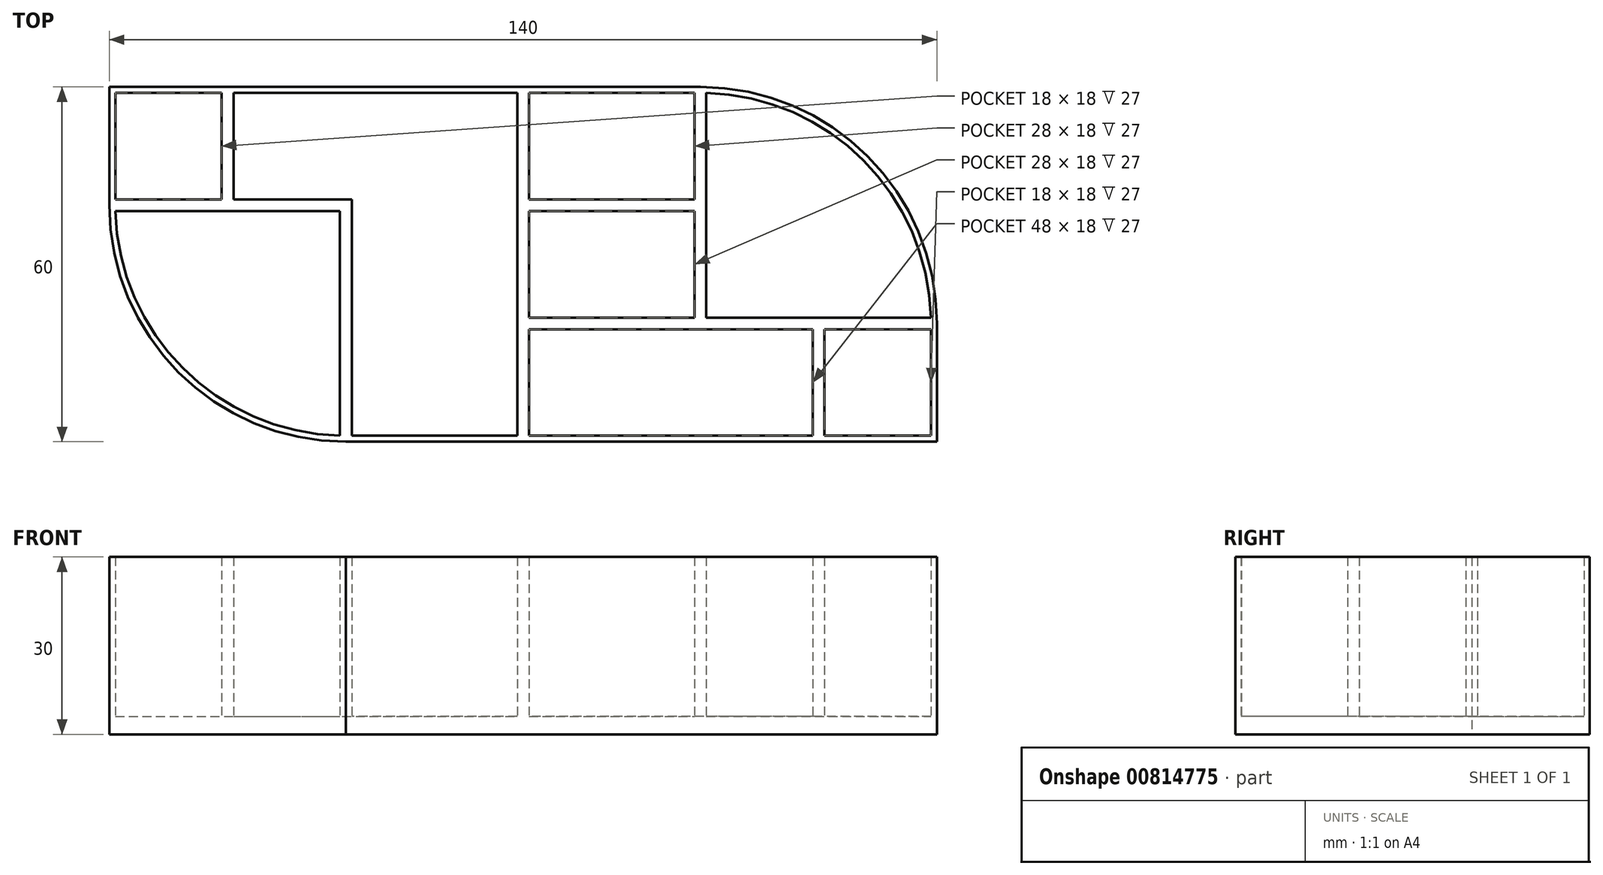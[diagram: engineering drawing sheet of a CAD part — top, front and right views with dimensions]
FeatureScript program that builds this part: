
annotation { "Feature Type Name" : "Feature", "Feature Type Description" : "" }
export const myFeature = defineFeature(function(context is Context, id is Id, definition is map)
    precondition{}
    {
        {
            var Q0;
            Q0=qCreatedBy(makeId("Top.planeOp"),FACE);
            var sketch = newSketch(context, id + "F0", { "sketchPlane" : qUnion([Q0])});
            skLineSegment(sketch, "E0.bottom", {"start": v(70, -30) * mm, "end": v(50, -30) * mm});
            skLineSegment(sketch, "E0.left", {"start": v(70, -30) * mm, "end": v(70, -10) * mm});
            skPoint(sketch, "E0.middle", {"position": v(0, 0) * mm});
            skLineSegment(sketch, "E1", {"start": v(0, 30) * mm, "end": v(0, 10) * mm});
            skLineSegment(sketch, "E2", {"start": v(0, -10) * mm, "end": v(30, -10) * mm});
            skLineSegment(sketch, "E3", {"start": v(0, 10) * mm, "end": v(30, 10) * mm});
            skLineSegment(sketch, "E4", {"start": v(50, -10) * mm, "end": v(50, -30) * mm});
            skLineSegment(sketch, "E5", {"start": v(30, -10) * mm, "end": v(30, -10) * mm});
            skLineSegment(sketch, "E6", {"start": v(-30, 10) * mm, "end": v(-30, -30) * mm});
            skLineSegment(sketch, "E7", {"start": v(-30, -30) * mm, "end": v(-30, -30) * mm});
            skLineSegment(sketch, "E8", {"start": v(-30, -30) * mm, "end": v(-30, -30) * mm});
            skLineSegment(sketch, "E9", {"start": v(30, 10) * mm, "end": v(30, 30) * mm});
            skLineSegment(sketch, "E10", {"start": v(70, -10) * mm, "end": v(70, -10) * mm});
            skLineSegment(sketch, "E11", {"start": v(-50, 30) * mm, "end": v(-70, 30) * mm});
            skLineSegment(sketch, "E12", {"start": v(-50, 10) * mm, "end": v(-30, 10) * mm});
            skLineSegment(sketch, "E13", {"start": v(-70, 10) * mm, "end": v(-70, 30) * mm});
            skLineSegment(sketch, "E14", {"start": v(-50, 10) * mm, "end": v(-50, 30) * mm});
            skLineSegment(sketch, "E15", {"start": v(-70, 10) * mm, "end": v(-50, 10) * mm});
            skArc(sketch, "E16", {"start": v(-70, 10) * mm, "mid": v(-58.28, -18.28) * mm, "end": v(-30, -30) * mm});
            skLineSegment(sketch, "E17", {"start": v(-30, -30) * mm, "end": v(-30, -30) * mm});
            skLineSegment(sketch, "E18.0", {"start": v(-51, 11) * mm, "end": v(-51, 29) * mm});
            skLineSegment(sketch, "E18.1", {"start": v(-69, 11) * mm, "end": v(-51, 11) * mm});
            skLineSegment(sketch, "E18.2", {"start": v(-69, 11) * mm, "end": v(-69, 29) * mm});
            skLineSegment(sketch, "E18.3", {"start": v(-51, 29) * mm, "end": v(-69, 29) * mm});
            skArc(sketch, "E19.0", {"start": v(-68.98, 9) * mm, "mid": v(-57.57, -17.57) * mm, "end": v(-31, -28.98) * mm});
            skLineSegment(sketch, "E19.1", {"start": v(-68.98, 9) * mm, "end": v(-50, 9) * mm});
            skLineSegment(sketch, "E19.2", {"start": v(-50, 9) * mm, "end": v(-31, 9) * mm});
            skLineSegment(sketch, "E19.3", {"start": v(-31, 9) * mm, "end": v(-31, -28.98) * mm});
            skLineSegment(sketch, "E20", {"start": v(-50, 30) * mm, "end": v(0, 30) * mm});
            skLineSegment(sketch, "E21", {"start": v(0, -30) * mm, "end": v(-30, -30) * mm});
            skLineSegment(sketch, "E22.0", {"start": v(-1, 29) * mm, "end": v(-1, -29) * mm});
            skLineSegment(sketch, "E22.1", {"start": v(-29, 11) * mm, "end": v(-29, -29) * mm});
            skLineSegment(sketch, "E22.2", {"start": v(-49, 11) * mm, "end": v(-29, 11) * mm});
            skLineSegment(sketch, "E22.3", {"start": v(-1, -29) * mm, "end": v(-29, -29) * mm});
            skLineSegment(sketch, "E22.4", {"start": v(-49, 11) * mm, "end": v(-49, 29) * mm});
            skLineSegment(sketch, "E22.5", {"start": v(-49, 29) * mm, "end": v(-1, 29) * mm});
            skLineSegment(sketch, "E23", {"start": v(0, 30) * mm, "end": v(30, 30) * mm});
            skArc(sketch, "E24", {"start": v(70, -10) * mm, "mid": v(58.28, 18.28) * mm, "end": v(30, 30) * mm});
            skLineSegment(sketch, "E25", {"start": v(30, -10) * mm, "end": v(30, 10) * mm});
            skLineSegment(sketch, "E26", {"start": v(30, -10) * mm, "end": v(50, -10) * mm});
            skLineSegment(sketch, "E27.0", {"start": v(31, -9) * mm, "end": v(68.99, -9) * mm});
            skLineSegment(sketch, "E27.1", {"start": v(31, -9) * mm, "end": v(31, 10) * mm});
            skLineSegment(sketch, "E27.2", {"start": v(31, 10) * mm, "end": v(31, 28.99) * mm});
            skArc(sketch, "E27.3", {"start": v(68.99, -9) * mm, "mid": v(57.58, 17.58) * mm, "end": v(31, 28.99) * mm});
            skLineSegment(sketch, "E28", {"start": v(0, 10) * mm, "end": v(0, -10) * mm});
            skLineSegment(sketch, "E29.0", {"start": v(1, 29) * mm, "end": v(1, 11) * mm});
            skLineSegment(sketch, "E29.1", {"start": v(1, 29) * mm, "end": v(29, 29) * mm});
            skLineSegment(sketch, "E29.2", {"start": v(29, 11) * mm, "end": v(29, 29) * mm});
            skLineSegment(sketch, "E29.3", {"start": v(1, 11) * mm, "end": v(29, 11) * mm});
            skLineSegment(sketch, "E30", {"start": v(0, -10) * mm, "end": v(0, -30) * mm});
            skLineSegment(sketch, "E31.0", {"start": v(1, -9) * mm, "end": v(29, -9) * mm});
            skLineSegment(sketch, "E31.1", {"start": v(1, 9) * mm, "end": v(1, -9) * mm});
            skLineSegment(sketch, "E31.2", {"start": v(1, 9) * mm, "end": v(29, 9) * mm});
            skLineSegment(sketch, "E31.3", {"start": v(29, -9) * mm, "end": v(29, 9) * mm});
            skLineSegment(sketch, "E32", {"start": v(50, -10) * mm, "end": v(70, -10) * mm});
            skLineSegment(sketch, "E33", {"start": v(50, -30) * mm, "end": v(0, -30) * mm});
            skLineSegment(sketch, "E34.0", {"start": v(69, -29) * mm, "end": v(51, -29) * mm});
            skLineSegment(sketch, "E34.1", {"start": v(69, -29) * mm, "end": v(69, -11) * mm});
            skLineSegment(sketch, "E34.2", {"start": v(51, -11) * mm, "end": v(69, -11) * mm});
            skLineSegment(sketch, "E34.3", {"start": v(51, -11) * mm, "end": v(51, -29) * mm});
            skLineSegment(sketch, "E35.0", {"start": v(49, -29) * mm, "end": v(1, -29) * mm});
            skLineSegment(sketch, "E35.1", {"start": v(49, -11) * mm, "end": v(49, -29) * mm});
            skLineSegment(sketch, "E35.2", {"start": v(1, -11) * mm, "end": v(1, -29) * mm});
            skLineSegment(sketch, "E35.3", {"start": v(1, -11) * mm, "end": v(30, -11) * mm});
            skLineSegment(sketch, "E35.4", {"start": v(30, -11) * mm, "end": v(49, -11) * mm});
            skSolve(sketch);
        }
        {
            var Q0;
            {var subQ4=sQuery(id+"F0.wireOp",EDGE,"E6");Q0=makeQuery(id+"F0.imprint","IMPRINT",FACE,{"disambiguationData":[TD([[makeQuery(id+"F0.imprint","IMPRINT",EDGE,{"derivedFrom":subQ4}),-1.0]])]});}
            var Q1;
            {var subQ0=sQuery(id+"F0.wireOp",EDGE,"KWAETHH6-OyeT-KhI5-DUXF-HT95SWmTHgVX");Q1=makeQuery(id+"F0.imprint","IMPRINT",FACE,{"disambiguationData":[TD([[makeQuery(id+"F0.imprint","IMPRINT",EDGE,{"derivedFrom":subQ0}),1.0]])]});}
            var Q2;
            {var subQ0=sQuery(id+"F0.wireOp",EDGE,"E0.right");var subQ1=sQuery(id+"F0.wireOp",EDGE,"E0.top");var subQ2=makeQuery(id+"F0.imprint","INTERSECT",VERTEX,{"derivedFrom":[subQ1,subQ0]});Q2=makeQuery(id+"F0.imprint","IMPRINT",FACE,{"disambiguationData":[TD([[makeQuery(id+"F0.imprint","IMPRINT",EDGE,{"disambiguationData":[TD([[subQ2,1.0]])],"derivedFrom":subQ1}),1.0]])]});}
            var Q3;
            {var subQ2=sQuery(id+"F0.wireOp",EDGE,"KWAETHH6-OyeT-KhI5-DUXF-HT95SWmTHgVX");Q3=makeQuery(id+"F0.imprint","IMPRINT",FACE,{"disambiguationData":[TD([[makeQuery(id+"F0.imprint","IMPRINT",EDGE,{"derivedFrom":subQ2}),-1.0]])]});}
            var Q4;
            {var subQ1=sQuery(id+"F0.wireOp",EDGE,"E1");var subQ7=makeQuery(id+"F0.imprint","INTERSECT",VERTEX,{"derivedFrom":[subQ1,sQuery(id+"F0.wireOp",EDGE,"E3")]});Q4=makeQuery(id+"F0.imprint","IMPRINT",FACE,{"disambiguationData":[TD([[makeQuery(id+"F0.imprint","IMPRINT",EDGE,{"disambiguationData":[TD([[subQ7,1.0]])],"derivedFrom":subQ1}),-1.0]])]});}
            var Q5;
            {var subQ0=sQuery(id+"F0.wireOp",EDGE,"E1");var subQ1=sQuery(id+"F0.wireOp",EDGE,"E0.bottom");var subQ2=makeQuery(id+"F0.imprint","INTERSECT",VERTEX,{"derivedFrom":[subQ1,subQ0]});Q5=makeQuery(id+"F0.imprint","IMPRINT",FACE,{"disambiguationData":[TD([[makeQuery(id+"F0.imprint","IMPRINT",EDGE,{"disambiguationData":[TD([[subQ2,-1.0]])],"derivedFrom":subQ1}),-1.0]])]});}
            var Q6;
            {var subQ1=sQuery(id+"F0.wireOp",EDGE,"E0.bottom");var subQ3=sQuery(id+"F0.wireOp",EDGE,"gBJW9aJL-3AMp-fhkF-frU9-a7ScvMq3sbXv");var subQ4=makeQuery(id+"F0.imprint","INTERSECT",VERTEX,{"disambiguationData":[OD(1.0)],"derivedFrom":[subQ1,subQ3]});Q6=makeQuery(id+"F0.imprint","IMPRINT",FACE,{"disambiguationData":[TD([[makeQuery(id+"F0.imprint","IMPRINT",EDGE,{"disambiguationData":[TD([[subQ4,1.0]])],"derivedFrom":subQ3}),-1.0]])]});}
            var Q7;
            {var subQ0=sQuery(id+"F0.wireOp",EDGE,"E4");Q7=makeQuery(id+"F0.imprint","IMPRINT",FACE,{"disambiguationData":[TD([[makeQuery(id+"F0.imprint","IMPRINT",EDGE,{"derivedFrom":subQ0}),-1.0]])]});}
            var Q8;
            {var subQ0=sQuery(id+"F0.wireOp",EDGE,"E5");var subQ1=sQuery(id+"F0.wireOp",EDGE,"E2");var subQ2=makeQuery(id+"F0.imprint","INTERSECT",VERTEX,{"derivedFrom":[subQ1,subQ0]});Q8=makeQuery(id+"F0.imprint","IMPRINT",FACE,{"disambiguationData":[TD([[makeQuery(id+"F0.imprint","IMPRINT",EDGE,{"disambiguationData":[TD([[subQ2,1.0]])],"derivedFrom":subQ1}),1.0]])]});}
            var Q9;
            {var subQ0=sQuery(id+"F0.wireOp",EDGE,"E2");var subQ1=sQuery(id+"F0.wireOp",EDGE,"E1");var subQ2=makeQuery(id+"F0.imprint","INTERSECT",VERTEX,{"derivedFrom":[subQ1,subQ0]});Q9=makeQuery(id+"F0.imprint","IMPRINT",FACE,{"disambiguationData":[TD([[makeQuery(id+"F0.imprint","IMPRINT",EDGE,{"disambiguationData":[TD([[subQ2,-1.0]])],"derivedFrom":subQ1}),1.0]])]});}
            var Q10;
            {var subQ0=sQuery(id+"F0.wireOp",EDGE,"E2");var subQ1=sQuery(id+"F0.wireOp",EDGE,"E1");var subQ2=makeQuery(id+"F0.imprint","INTERSECT",VERTEX,{"derivedFrom":[subQ1,subQ0]});Q10=makeQuery(id+"F0.imprint","IMPRINT",FACE,{"disambiguationData":[TD([[makeQuery(id+"F0.imprint","IMPRINT",EDGE,{"disambiguationData":[TD([[subQ2,1.0]])],"derivedFrom":subQ1}),1.0]])]});}
            var Q11;
            {var subQ0=sQuery(id+"F0.wireOp",EDGE,"E3");var subQ1=sQuery(id+"F0.wireOp",EDGE,"E1");var subQ2=makeQuery(id+"F0.imprint","INTERSECT",VERTEX,{"derivedFrom":[subQ1,subQ0]});Q11=makeQuery(id+"F0.imprint","IMPRINT",FACE,{"disambiguationData":[TD([[makeQuery(id+"F0.imprint","IMPRINT",EDGE,{"disambiguationData":[TD([[subQ2,1.0]])],"derivedFrom":subQ1}),1.0]])]});}
            var Q12;
            {var subQ0=sQuery(id+"F0.wireOp",EDGE,"E1");var subQ1=sQuery(id+"F0.wireOp",EDGE,"E0.top");var subQ2=makeQuery(id+"F0.imprint","INTERSECT",VERTEX,{"derivedFrom":[subQ1,subQ0]});Q12=makeQuery(id+"F0.imprint","IMPRINT",FACE,{"disambiguationData":[TD([[makeQuery(id+"F0.imprint","IMPRINT",EDGE,{"disambiguationData":[TD([[subQ2,1.0]])],"derivedFrom":subQ1}),1.0]])]});}
            var Q13;
            {var subQ0=sQuery(id+"F0.wireOp",EDGE,"b8PX1bvO-8tuv-nnMc-ZB4T-NcWpUWVzeNnX");var subQ1=sQuery(id+"F0.wireOp",EDGE,"E3");var subQ2=makeQuery(id+"F0.imprint","INTERSECT",VERTEX,{"derivedFrom":[subQ1,subQ0]});Q13=makeQuery(id+"F0.imprint","IMPRINT",FACE,{"disambiguationData":[TD([[makeQuery(id+"F0.imprint","IMPRINT",EDGE,{"disambiguationData":[TD([[subQ2,-1.0]])],"derivedFrom":subQ1}),1.0]])]});}
            var Q14;
            {var subQ1=sQuery(id+"F0.wireOp",EDGE,"E0.top");var subQ3=sQuery(id+"F0.wireOp",EDGE,"b8PX1bvO-8tuv-nnMc-ZB4T-NcWpUWVzeNnX");var subQ4=makeQuery(id+"F0.imprint","INTERSECT",VERTEX,{"disambiguationData":[OD(0.0)],"derivedFrom":[subQ1,subQ3]});Q14=makeQuery(id+"F0.imprint","IMPRINT",FACE,{"disambiguationData":[TD([[makeQuery(id+"F0.imprint","IMPRINT",EDGE,{"disambiguationData":[TD([[subQ4,1.0]])],"derivedFrom":subQ3}),-1.0]])]});}
            var Q15;
            {var subQ0=sQuery(id+"F0.wireOp",EDGE,"E5");var subQ1=sQuery(id+"F0.wireOp",EDGE,"E3");var subQ2=makeQuery(id+"F0.imprint","INTERSECT",VERTEX,{"derivedFrom":[subQ1,subQ0]});Q15=makeQuery(id+"F0.imprint","IMPRINT",FACE,{"disambiguationData":[TD([[makeQuery(id+"F0.imprint","IMPRINT",EDGE,{"disambiguationData":[TD([[subQ2,-1.0]])],"derivedFrom":subQ1}),1.0]])]});}
            var Q16;
            {var subQ1=sQuery(id+"F0.wireOp",EDGE,"E2");var subQ8=makeQuery(id+"F0.imprint","INTERSECT",VERTEX,{"derivedFrom":[subQ1,sQuery(id+"F0.wireOp",EDGE,"E4")]});Q16=makeQuery(id+"F0.imprint","IMPRINT",FACE,{"disambiguationData":[TD([[makeQuery(id+"F0.imprint","IMPRINT",EDGE,{"disambiguationData":[TD([[subQ8,1.0]])],"derivedFrom":subQ1}),1.0]])]});}
            var Q17;
            {var subQ0=sQuery(id+"F0.wireOp",EDGE,"E4");Q17=makeQuery(id+"F0.imprint","IMPRINT",FACE,{"disambiguationData":[TD([[makeQuery(id+"F0.imprint","IMPRINT",EDGE,{"derivedFrom":subQ0}),1.0]])]});}
            var Q18;
            {var subQ0=sQuery(id+"F0.wireOp",EDGE,"E0.left");var subQ1=sQuery(id+"F0.wireOp",EDGE,"E0.bottom");var subQ2=makeQuery(id+"F0.imprint","INTERSECT",VERTEX,{"derivedFrom":[subQ1,subQ0]});Q18=makeQuery(id+"F0.imprint","IMPRINT",FACE,{"disambiguationData":[TD([[makeQuery(id+"F0.imprint","IMPRINT",EDGE,{"disambiguationData":[TD([[subQ2,-1.0]])],"derivedFrom":subQ1}),-1.0]])]});}
            var Q19;
            Q19=makeQuery(id+"F0.imprint","IMPRINT",FACE,{"disambiguationData":[TD([[makeQuery(id+"F0.imprint","IMPRINT",EDGE,{"derivedFrom":sQuery(id+"F0.wireOp",EDGE,"E11")}),1.0]])]});
            var Q20;
            Q20=makeQuery(id+"F0.imprint","IMPRINT",FACE,{"disambiguationData":[TD([[makeQuery(id+"F0.imprint","IMPRINT",EDGE,{"derivedFrom":sQuery(id+"F0.wireOp",EDGE,"E9")}),-1.0]])]});
            extrude(context, id + "F1", {"entities" : qUnion([Q0, Q1, Q2, Q3, Q4, Q5, Q6, Q7, Q8, Q9, Q10, Q11, Q12, Q13, Q14, Q15, Q16, Q17, Q18, Q19, Q20]), "depth" : 30 * mm, "offsetDistance" : 25 * mm});
        }
        {
            var Q0;
            Q0=makeQuery(id+"F0.imprint","IMPRINT",FACE,{"disambiguationData":[TD([[makeQuery(id+"F0.imprint","IMPRINT",EDGE,{"derivedFrom":sQuery(id+"F0.wireOp",EDGE,"E18.0")}),1.0]])]});
            var Q1;
            Q1=makeQuery(id+"F0.imprint","IMPRINT",FACE,{"disambiguationData":[TD([[makeQuery(id+"F0.imprint","IMPRINT",EDGE,{"derivedFrom":sQuery(id+"F0.wireOp",EDGE,"E22.0")}),-1.0]])]});
            var Q2;
            Q2=makeQuery(id+"F0.imprint","IMPRINT",FACE,{"disambiguationData":[TD([[makeQuery(id+"F0.imprint","IMPRINT",EDGE,{"derivedFrom":sQuery(id+"F0.wireOp",EDGE,"E19.0")}),1.0]])]});
            var Q3;
            {var subQ4=sQuery(id+"F0.wireOp",EDGE,"6c6feae6-9f81-4454-8293-936d37830c75.1");Q3=makeQuery(id+"F0.imprint","IMPRINT",FACE,{"disambiguationData":[TD([[makeQuery(id+"F0.imprint","IMPRINT",EDGE,{"derivedFrom":subQ4}),1.0]])]});}
            var Q4;
            Q4=makeQuery(id+"F0.imprint","IMPRINT",FACE,{"disambiguationData":[TD([[makeQuery(id+"F0.imprint","IMPRINT",EDGE,{"derivedFrom":sQuery(id+"F0.wireOp",EDGE,"E31.0")}),1.0]])]});
            var Q5;
            Q5=makeQuery(id+"F0.imprint","IMPRINT",FACE,{"disambiguationData":[TD([[makeQuery(id+"F0.imprint","IMPRINT",EDGE,{"derivedFrom":sQuery(id+"F0.wireOp",EDGE,"E29.0")}),1.0]])]});
            var Q6;
            Q6=makeQuery(id+"F0.imprint","IMPRINT",FACE,{"disambiguationData":[TD([[makeQuery(id+"F0.imprint","IMPRINT",EDGE,{"derivedFrom":sQuery(id+"F0.wireOp",EDGE,"E27.0")}),1.0]])]});
            var Q7;
            {var subQ5=sQuery(id+"F0.wireOp",EDGE,"6c6feae6-9f81-4454-8293-936d37830c75.2");Q7=makeQuery(id+"F0.imprint","IMPRINT",FACE,{"disambiguationData":[TD([[makeQuery(id+"F0.imprint","IMPRINT",EDGE,{"derivedFrom":subQ5}),1.0]])]});}
            var Q8;
            Q8=makeQuery(id+"F0.imprint","IMPRINT",FACE,{"disambiguationData":[TD([[makeQuery(id+"F0.imprint","IMPRINT",EDGE,{"derivedFrom":sQuery(id+"F0.wireOp",EDGE,"E35.0")}),-1.0]])]});
            var Q9;
            Q9=makeQuery(id+"F0.imprint","IMPRINT",FACE,{"disambiguationData":[TD([[makeQuery(id+"F0.imprint","IMPRINT",EDGE,{"derivedFrom":sQuery(id+"F0.wireOp",EDGE,"E34.0")}),-1.0]])]});
            extrude(context, id + "F2", {"entities" : qUnion([Q0, Q1, Q2, Q3, Q4, Q5, Q6, Q7, Q8, Q9]), "operationType" : NewBodyOperationType.ADD, "depth" : 3 * mm, "offsetDistance" : 25 * mm});
        }
    });
